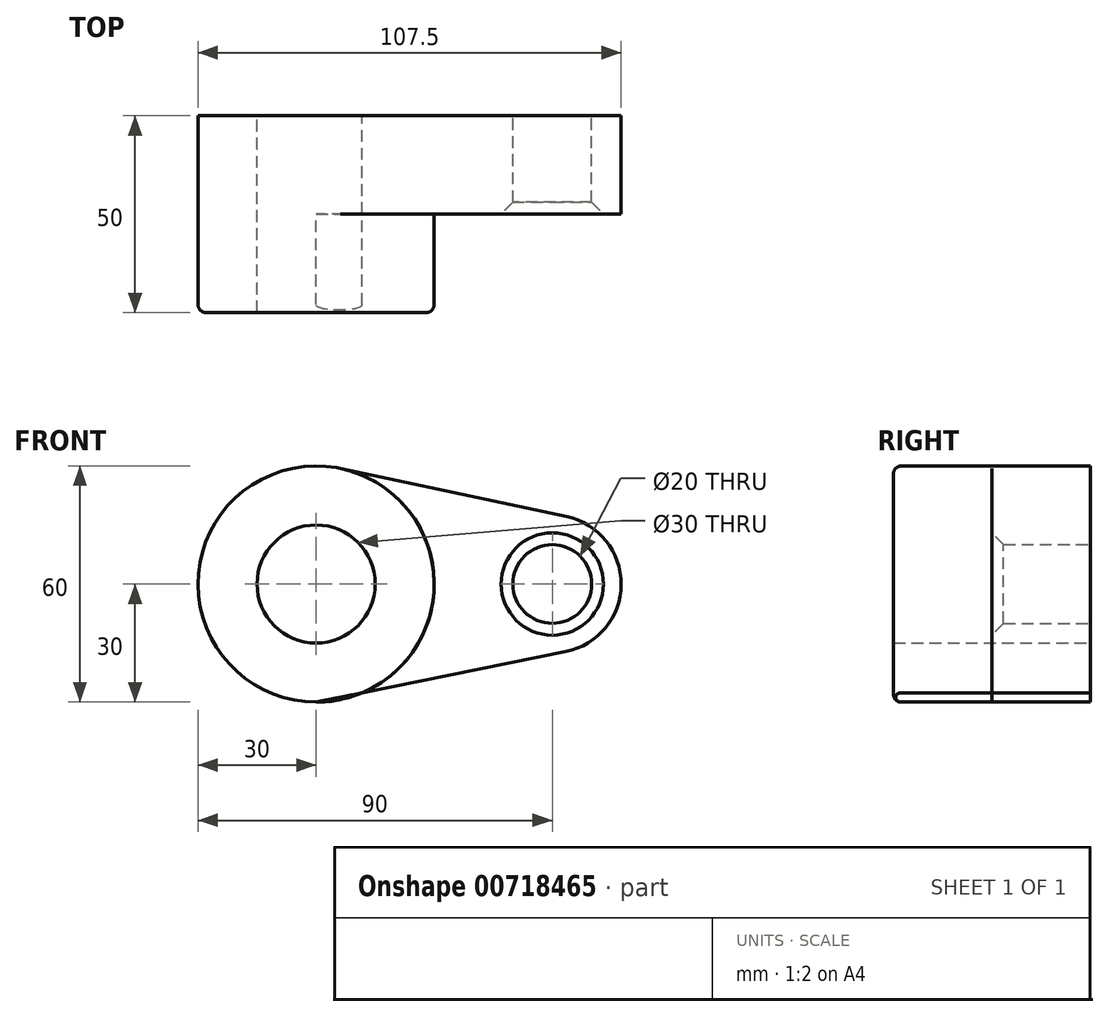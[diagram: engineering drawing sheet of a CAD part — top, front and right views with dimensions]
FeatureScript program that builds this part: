
annotation { "Feature Type Name" : "Feature", "Feature Type Description" : "" }
export const myFeature = defineFeature(function(context is Context, id is Id, definition is map)
    precondition{}
    {
        {
            var Q0;
            Q0=qCreatedBy(makeId("Front.planeOp"),FACE);
            var sketch = newSketch(context, id + "F0", { "sketchPlane" : qUnion([Q0])});
            skCircle(sketch, "E0", {"center": v(0, 0) * mm, "radius": 30 * mm});
            skCircle(sketch, "E1", {"center": v(60, 0) * mm, "radius": 17.5 * mm});
            skLineSegment(sketch, "E2", {"start": v(6.25, 29.34) * mm, "end": v(63.65, 17.12) * mm});
            skLineSegment(sketch, "E3", {"start": v(0, -30) * mm, "end": v(63.65, -17.12) * mm});
            skCircle(sketch, "E4", {"center": v(0, 0) * mm, "radius": 15 * mm});
            skCircle(sketch, "E5", {"center": v(60, 0) * mm, "radius": 10 * mm});
            skSolve(sketch);
        }
        {
            var Q0;
            Q0 = qSketchRegion(id + "F0", true);
            extrude(context, id + "F1", {"entities" : qUnion([Q0]), "depth" : 25 * mm, "offsetDistance" : 25 * mm});
        }
        {
            var Q0;
            Q0=makeQuery(id+"F0.imprint","IMPRINT",FACE,{"disambiguationData":[TD([[makeQuery(id+"F0.imprint","IMPRINT",EDGE,{"derivedFrom":sQuery(id+"F0.wireOp",EDGE,"E4")}),-1.0]])]});
            extrude(context, id + "F2", {"entities" : qUnion([Q0]), "operationType" : NewBodyOperationType.ADD, "depth" : 50 * mm, "offsetDistance" : 25 * mm});
        }
        {
            var Q0;
            Q0=makeQuery(id+"F2.opExtrude","CAP_EDGE",EDGE,{"disambiguationData":[OSD([sQuery(id+"F0.wireOp",EDGE,"E0")])],"isStart":false});
            fillet(context, id + "F3", {"entities" : qUnion([Q0]), "radius" : 2 * mm, "tangentPropagation" : true, "allowEdgeOverflow" : false});
        }
        {
            var Q0;
            Q0=makeQuery(id+"F1.opExtrude","CAP_EDGE",EDGE,{"disambiguationData":[OSD([sQuery(id+"F0.wireOp",EDGE,"E5")])],"isStart":false});
            chamfer(context, id + "F4", {"entities" : qUnion([Q0]), "width" : 3 * mm, "tangentPropagation" : true});
        }
    });
